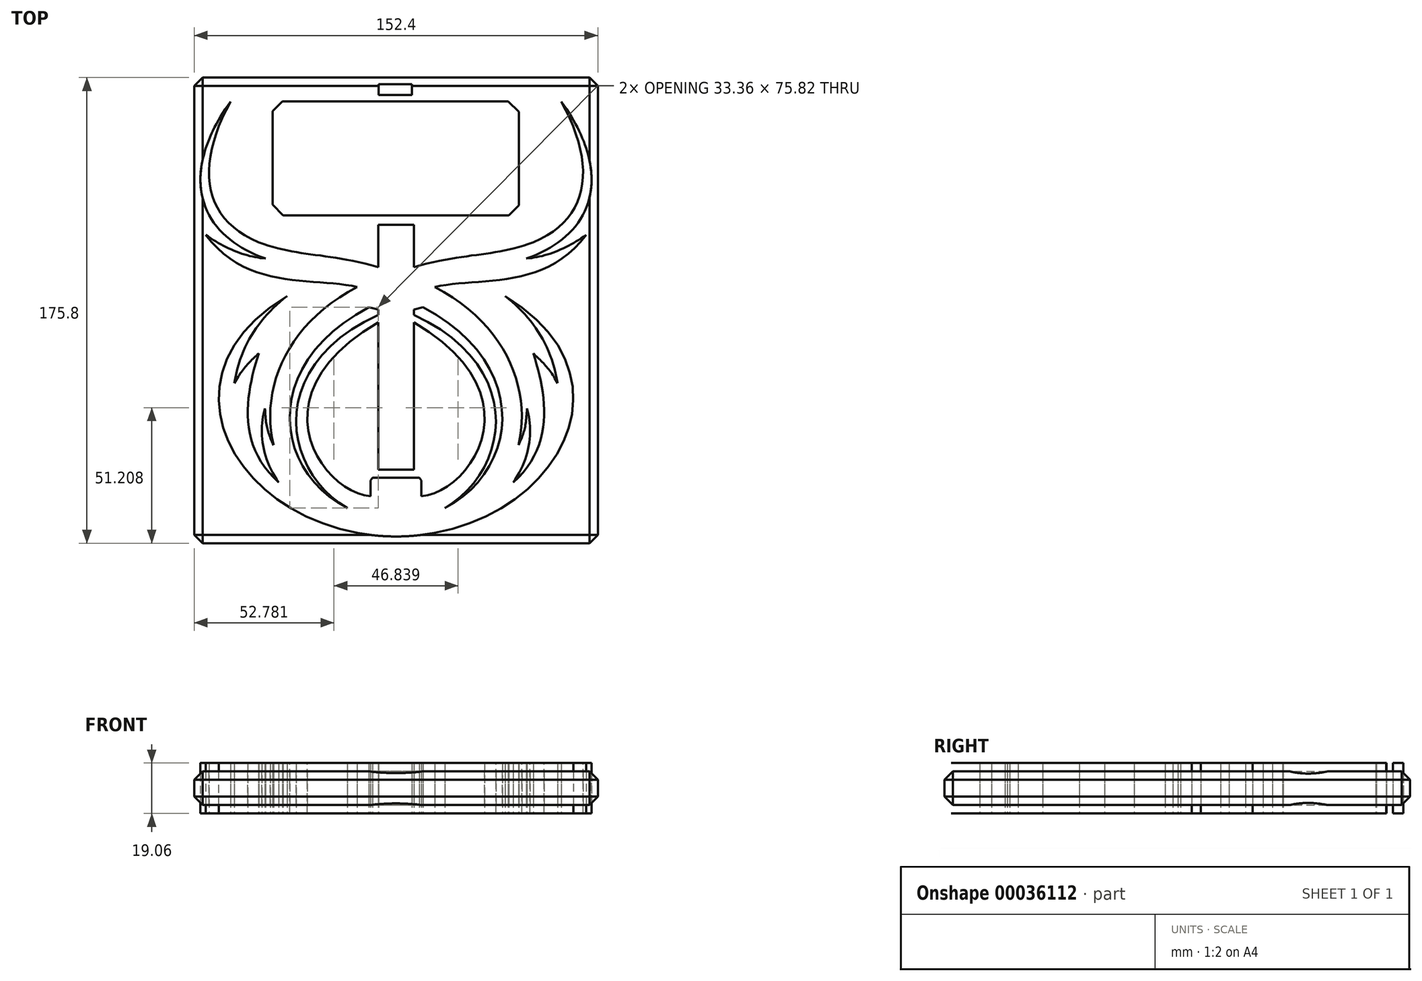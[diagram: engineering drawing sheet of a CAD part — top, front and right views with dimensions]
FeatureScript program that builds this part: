
annotation { "Feature Type Name" : "Feature", "Feature Type Description" : "" }
export const myFeature = defineFeature(function(context is Context, id is Id, definition is map)
    precondition{}
    {
        {
            var Q0;
            Q0=qCreatedBy(makeId("Top.planeOp"),FACE);
            var sketch = newSketch(context, id + "F0", { "sketchPlane" : qUnion([Q0])});
            skLineSegment(sketch, "E0", {"start": v(-42.98, 90.94) * mm, "end": v(-46.75, 87.16) * mm});
            skLineSegment(sketch, "E1", {"start": v(-46.75, 87.16) * mm, "end": v(-46.75, 51.9) * mm});
            skLineSegment(sketch, "E2", {"start": v(-46.75, 51.9) * mm, "end": v(-42.74, 47.88) * mm});
            skLineSegment(sketch, "E3", {"start": v(-42.74, 47.88) * mm, "end": v(42.46, 47.88) * mm});
            skLineSegment(sketch, "E4", {"start": v(42.46, 47.88) * mm, "end": v(46.23, 51.65) * mm});
            skLineSegment(sketch, "E5", {"start": v(46.23, 51.65) * mm, "end": v(46.23, 86.92) * mm});
            skLineSegment(sketch, "E6", {"start": v(46.23, 86.92) * mm, "end": v(42.22, 90.94) * mm});
            skLineSegment(sketch, "E7", {"start": v(42.22, 90.94) * mm, "end": v(-42.98, 90.94) * mm});
            skLineSegment(sketch, "E8", {"start": v(-0.14, 44.29) * mm, "end": v(-6.88, 44.29) * mm});
            skLineSegment(sketch, "E9", {"start": v(-0.14, 44.29) * mm, "end": v(6.6, 44.29) * mm});
            skLineSegment(sketch, "E10", {"start": v(6.6, 44.29) * mm, "end": v(6.6, -48.14) * mm});
            skLineSegment(sketch, "E11", {"start": v(6.6, -48.14) * mm, "end": v(-0.14, -48.14) * mm});
            skLineSegment(sketch, "E12", {"start": v(-0.14, -48.14) * mm, "end": v(-6.88, -48.14) * mm});
            skLineSegment(sketch, "E13", {"start": v(-6.88, -48.14) * mm, "end": v(-6.88, 44.29) * mm});
            skFitSpline(sketch, "E14", {"points": [v(-6.88, 28.3) * mm, v(-52.06, 37.7) * mm], "startDerivative": vector(-59.97, 17) * mm, "endDerivative": vector(-44.06, 16.78) * mm});
            skFitSpline(sketch, "E15", {"points": [v(-52.06, 37.7) * mm, v(-62.6, 90.76) * mm], "startDerivative": vector(-63.94, 26.98) * mm, "endDerivative": vector(39.71, 72.22) * mm});
            skFitSpline(sketch, "E16", {"points": [v(-62.6, 90.76) * mm, v(-49.4, 31.56) * mm], "startDerivative": vector(-62.97, -87.47) * mm, "endDerivative": vector(71.94, -24.51) * mm});
            skFitSpline(sketch, "E17", {"points": [v(-49.4, 31.56) * mm, v(-71.92, 40.42) * mm], "startDerivative": vector(-22.2, 1.47) * mm, "endDerivative": vector(-20.78, 14.7) * mm});
            skFitSpline(sketch, "E18", {"points": [v(-71.92, 40.42) * mm, v(-14.8, 20.8) * mm], "startDerivative": vector(47.65, -63.79) * mm, "endDerivative": vector(47.3, -11.36) * mm});
            skFitSpline(sketch, "E19", {"points": [v(-14.8, 20.8) * mm, v(-46.37, -38.85) * mm], "startDerivative": vector(-81.16, -41.99) * mm, "endDerivative": vector(14.94, -61.77) * mm});
            skFitSpline(sketch, "E20", {"points": [v(-46.37, -38.85) * mm, v(-49.58, -25.06) * mm], "startDerivative": vector(-6.78, 14.04) * mm, "endDerivative": vector(-0.79, 19.86) * mm});
            skFitSpline(sketch, "E21", {"points": [v(-49.58, -25.06) * mm, v(-44.36, -53.06) * mm], "startDerivative": vector(-7.29, -23.63) * mm, "endDerivative": vector(19.93, -27.9) * mm});
            skFitSpline(sketch, "E22", {"points": [v(-44.36, -53.06) * mm, v(-51.97, -4.28) * mm], "startDerivative": vector(-48.67, 43.83) * mm, "endDerivative": vector(14.29, 45.51) * mm});
            skFitSpline(sketch, "E23", {"points": [v(-51.97, -4.28) * mm, v(-61.12, -15.49) * mm], "startDerivative": vector(-9.77, -8.9) * mm, "endDerivative": vector(-7.8, -15.01) * mm});
            skFitSpline(sketch, "E24", {"points": [v(-61.12, -15.49) * mm, v(-41.29, 17.4) * mm], "startDerivative": vector(6.94, 43.02) * mm, "endDerivative": vector(31.56, 24.95) * mm});
            skFitSpline(sketch, "E25", {"points": [v(-41.29, 17.4) * mm, v(-0.14, -73.42) * mm], "startDerivative": vector(-159.4, -95.84) * mm, "endDerivative": vector(173.06, -0.83) * mm});
            skLineSegment(sketch, "E26", {"start": v(-0.14, 44.29) * mm, "end": v(-0.14, 25.92) * mm});
            skFitSpline(sketch, "E27.MirrorCS", {"points": [v(6.6, 28.3) * mm, v(51.78, 37.7) * mm], "startDerivative": vector(59.97, 17) * mm, "endDerivative": vector(44.06, 16.78) * mm});
            skFitSpline(sketch, "E28.MirrorCS", {"points": [v(51.78, 37.7) * mm, v(62.32, 90.76) * mm], "startDerivative": vector(63.94, 26.98) * mm, "endDerivative": vector(-39.71, 72.22) * mm});
            skFitSpline(sketch, "E29.MirrorCS", {"points": [v(62.32, 90.76) * mm, v(49.11, 31.56) * mm], "startDerivative": vector(62.97, -87.47) * mm, "endDerivative": vector(-71.94, -24.51) * mm});
            skFitSpline(sketch, "E30.MirrorCS", {"points": [v(49.11, 31.56) * mm, v(71.64, 40.42) * mm], "startDerivative": vector(22.2, 1.47) * mm, "endDerivative": vector(20.78, 14.7) * mm});
            skFitSpline(sketch, "E31.MirrorCS", {"points": [v(71.64, 40.42) * mm, v(14.53, 20.8) * mm], "startDerivative": vector(-47.65, -63.79) * mm, "endDerivative": vector(-47.3, -11.36) * mm});
            skFitSpline(sketch, "E32.MirrorCS", {"points": [v(14.53, 20.8) * mm, v(46.1, -38.85) * mm], "startDerivative": vector(81.16, -41.99) * mm, "endDerivative": vector(-14.94, -61.77) * mm});
            skFitSpline(sketch, "E33.MirrorCS", {"points": [v(46.1, -38.85) * mm, v(49.3, -25.06) * mm], "startDerivative": vector(6.78, 14.04) * mm, "endDerivative": vector(0.79, 19.86) * mm});
            skFitSpline(sketch, "E34.MirrorCS", {"points": [v(49.3, -25.06) * mm, v(44.08, -53.06) * mm], "startDerivative": vector(7.29, -23.63) * mm, "endDerivative": vector(-19.93, -27.9) * mm});
            skFitSpline(sketch, "E35.MirrorCS", {"points": [v(44.08, -53.06) * mm, v(51.7, -4.28) * mm], "startDerivative": vector(48.67, 43.83) * mm, "endDerivative": vector(-14.29, 45.51) * mm});
            skFitSpline(sketch, "E36.MirrorCS", {"points": [v(51.7, -4.28) * mm, v(60.84, -15.49) * mm], "startDerivative": vector(9.77, -8.9) * mm, "endDerivative": vector(7.8, -15.01) * mm});
            skFitSpline(sketch, "E37.MirrorCS", {"points": [v(60.84, -15.49) * mm, v(41, 17.4) * mm], "startDerivative": vector(-6.94, 43.02) * mm, "endDerivative": vector(-31.56, 24.95) * mm});
            skFitSpline(sketch, "E38.MirrorCS", {"points": [v(41, 17.4) * mm, v(-0.14, -73.42) * mm], "startDerivative": vector(159.4, -95.84) * mm, "endDerivative": vector(-173.06, -0.83) * mm});
            skLineSegment(sketch, "E39", {"start": v(-6.88, 12.24) * mm, "end": v(-10.36, 13.16) * mm});
            skFitSpline(sketch, "E40", {"points": [v(-10.36, 13.16) * mm, v(-18.57, -62.66) * mm], "startDerivative": vector(-121.46, -63.51) * mm, "endDerivative": vector(84.75, -43.83) * mm});
            skFitSpline(sketch, "E41", {"points": [v(-6.88, 10.25) * mm, v(-18.57, -62.66) * mm], "startDerivative": vector(-127.92, -58.87) * mm, "endDerivative": vector(72.8, -42.55) * mm});
            skFitSpline(sketch, "E42", {"points": [v(-6.88, 7.4) * mm, v(-9.78, -58.15) * mm], "startDerivative": vector(-142.1, -81.91) * mm, "endDerivative": vector(54.06, -3.6) * mm});
            skLineSegment(sketch, "E43", {"start": v(-9.78, -58.15) * mm, "end": v(-9.78, -52.23) * mm});
            skLineSegment(sketch, "E44", {"start": v(-9.78, -52.23) * mm, "end": v(-8.92, -51.29) * mm});
            skLineSegment(sketch, "E45", {"start": v(-8.92, -51.29) * mm, "end": v(-0.14, -51.29) * mm});
            skFitSpline(sketch, "E46.MirrorCS", {"points": [v(6.6, 7.4) * mm, v(9.5, -58.15) * mm], "startDerivative": vector(142.1, -81.91) * mm, "endDerivative": vector(-54.06, -3.6) * mm});
            skFitSpline(sketch, "E47.MirrorCS", {"points": [v(6.6, 10.25) * mm, v(18.29, -62.66) * mm], "startDerivative": vector(127.92, -58.87) * mm, "endDerivative": vector(-72.8, -42.55) * mm});
            skLineSegment(sketch, "E48.MirrorCS", {"start": v(8.64, -51.29) * mm, "end": v(-0.14, -51.29) * mm});
            skLineSegment(sketch, "E49.MirrorCS", {"start": v(9.5, -52.23) * mm, "end": v(8.64, -51.29) * mm});
            skLineSegment(sketch, "E50.MirrorCS", {"start": v(9.5, -58.15) * mm, "end": v(9.5, -52.23) * mm});
            skFitSpline(sketch, "E51.MirrorCS", {"points": [v(10.08, 13.16) * mm, v(18.29, -62.66) * mm], "startDerivative": vector(121.46, -63.51) * mm, "endDerivative": vector(-84.75, -43.83) * mm});
            skLineSegment(sketch, "E52.MirrorCS", {"start": v(6.6, 12.24) * mm, "end": v(10.08, 13.16) * mm});
            skLineSegment(sketch, "E53", {"start": v(-0.38, 93.35) * mm, "end": v(-6.65, 93.35) * mm});
            skPoint(sketch, "E53.startSnap0", {"position": v(-0.38, 90.94) * mm});
            skLineSegment(sketch, "E54", {"start": v(-6.65, 93.35) * mm, "end": v(-6.65, 97.3) * mm});
            skLineSegment(sketch, "E55", {"start": v(-6.65, 97.3) * mm, "end": v(-0.38, 97.3) * mm});
            skLineSegment(sketch, "E56.MirrorCS", {"start": v(5.9, 97.3) * mm, "end": v(-0.38, 97.3) * mm});
            skLineSegment(sketch, "E57.MirrorCS", {"start": v(5.9, 93.35) * mm, "end": v(5.9, 97.3) * mm});
            skLineSegment(sketch, "E58.MirrorCS", {"start": v(-0.38, 93.35) * mm, "end": v(5.9, 93.35) * mm});
            skLineSegment(sketch, "E59", {"start": v(-0.14, -73.42) * mm, "end": v(-0.14, -75.96) * mm});
            skLineSegment(sketch, "E60", {"start": v(-0.14, -75.96) * mm, "end": v(76.06, -75.96) * mm});
            skLineSegment(sketch, "E61", {"start": v(-0.14, -75.96) * mm, "end": v(-76.34, -75.96) * mm});
            skLineSegment(sketch, "E62", {"start": v(-0.38, 97.3) * mm, "end": v(-0.38, 99.84) * mm});
            skLineSegment(sketch, "E63", {"start": v(-0.38, 99.84) * mm, "end": v(-76.34, 99.84) * mm});
            skLineSegment(sketch, "E64", {"start": v(-76.34, 99.84) * mm, "end": v(-76.34, -75.96) * mm});
            skLineSegment(sketch, "E65", {"start": v(-0.38, 99.84) * mm, "end": v(76.06, 99.84) * mm});
            skLineSegment(sketch, "E66", {"start": v(76.06, 99.84) * mm, "end": v(76.06, -75.96) * mm});
            skLineSegment(sketch, "E67", {"start": v(-73.97, 73) * mm, "end": v(-73.97, 55.9) * mm});
            skLineSegment(sketch, "E68", {"start": v(73.69, 71.18) * mm, "end": v(73.69, 49.6) * mm});
            skSolve(sketch);
        }
        {
            var Q0;
            Q0=makeQuery(id+"F0.imprint","IMPRINT",FACE,{"disambiguationData":[TD([[makeQuery(id+"F0.imprint","IMPRINT",EDGE,{"derivedFrom":sQuery(id+"F0.wireOp",EDGE,"E0")}),-1.0]])]});
            var Q1;
            {var subQ1=sQuery(id+"F0.wireOp",EDGE,"E47.MirrorCS");Q1=makeQuery(id+"F0.imprint","IMPRINT",FACE,{"disambiguationData":[TD([[makeQuery(id+"F0.imprint","IMPRINT",EDGE,{"derivedFrom":subQ1}),1.0]])]});}
            var Q2;
            {var subQ1=sQuery(id+"F0.wireOp",EDGE,"E39");Q2=makeQuery(id+"F0.imprint","IMPRINT",FACE,{"disambiguationData":[TD([[makeQuery(id+"F0.imprint","IMPRINT",EDGE,{"derivedFrom":subQ1}),1.0]])]});}
            var Q3;
            {var subQ4=sQuery(id+"F0.wireOp",EDGE,"E11");Q3=makeQuery(id+"F0.imprint","IMPRINT",FACE,{"disambiguationData":[TD([[makeQuery(id+"F0.imprint","IMPRINT",EDGE,{"derivedFrom":subQ4}),1.0]])]});}
            extrude(context, id + "F1", {"entities" : qUnion([Q0, Q1, Q2, Q3]), "endBound" : BoundingType.SYMMETRIC, "depth" : 12.7 * mm});
        }
        {
            var Q0;
            Q0=makeQuery(id+"F0.imprint","IMPRINT",FACE,{"disambiguationData":[TD([[makeQuery(id+"F0.imprint","IMPRINT",EDGE,{"derivedFrom":sQuery(id+"F0.wireOp",EDGE,"E0")}),1.0]])]});
            var Q1;
            Q1=makeQuery(id+"F0.imprint","IMPRINT",FACE,{"disambiguationData":[TD([[makeQuery(id+"F0.imprint","IMPRINT",EDGE,{"derivedFrom":sQuery(id+"F0.wireOp",EDGE,"E53")}),-1.0]])]});
            var Q2;
            {var subQ2=sQuery(id+"F0.wireOp",EDGE,"E8");Q2=makeQuery(id+"F0.imprint","IMPRINT",FACE,{"disambiguationData":[TD([[makeQuery(id+"F0.imprint","IMPRINT",EDGE,{"derivedFrom":subQ2}),1.0]])]});}
            var Q3;
            {var subQ9=sQuery(id+"F0.wireOp",EDGE,"E14");Q3=makeQuery(id+"F0.imprint","IMPRINT",FACE,{"disambiguationData":[TD([[makeQuery(id+"F0.imprint","IMPRINT",EDGE,{"derivedFrom":subQ9}),1.0]])]});}
            extrude(context, id + "F2", {"entities" : qUnion([Q0, Q1, Q2, Q3]), "endBound" : BoundingType.SYMMETRIC, "depth" : 19.05 * mm});
        }
        {
            var Q0;
            Q0=makeQuery(id+"F1.opExtrude","SWEPT_FACE",FACE,{"disambiguationData":[OSD([sQuery(id+"F0.wireOp",EDGE,"E66")])]});
            var Q1;
            Q1=makeQuery(id+"F1.opExtrude","SWEPT_FACE",FACE,{"disambiguationData":[OSD([sQuery(id+"F0.wireOp",EDGE,"E64")])]});
            var Q2;
            Q2=makeQuery(id+"F1.opExtrude","SWEPT_FACE",FACE,{"disambiguationData":[OSD([sQuery(id+"F0.wireOp",EDGE,"E63"),sQuery(id+"F0.wireOp",EDGE,"E65")])]});
            var Q3;
            Q3=makeQuery(id+"F1.opExtrude","SWEPT_FACE",FACE,{"disambiguationData":[OSD([sQuery(id+"F0.wireOp",EDGE,"E60"),sQuery(id+"F0.wireOp",EDGE,"E61")])]});
            chamfer(context, id + "F3", {"entities" : qUnion([Q0, Q1, Q2, Q3]), "width" : 3.17 * mm, "tangentPropagation" : true});
        }
    });
